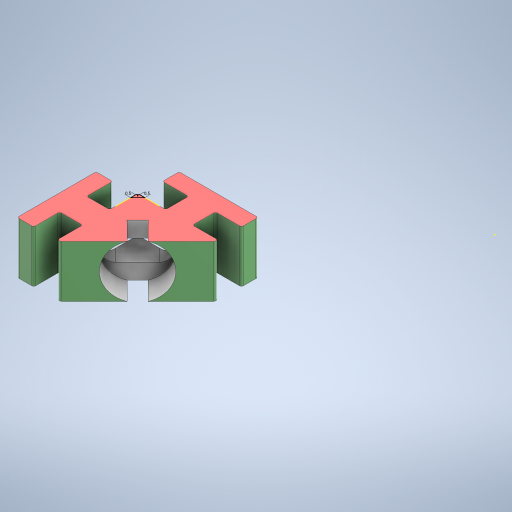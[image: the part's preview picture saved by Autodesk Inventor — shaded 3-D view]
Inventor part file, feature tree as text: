
AUTODESK INVENTOR PART (.ipt)
format: ipt  version: 2023 (Build 270158000, 158)  size: 336,384 bytes
history: native  units: in
note: dims shown in document units (in); Inventor stores cm internally (conversion verified against a paired STEP export)
features: other x4, sketch x3, extrude x2
ambient origin geometry x8: Origin, YZ Plane, XZ Plane, XY Plane, X Axis, Y Axis, Z Axis, Center Point
bodies: Body1 (feature_tree)
feature tree (9):
  other  "TmpPart3.ipt"
  extrude  "Extrusion1"  Depth=0.3937in
  extrude  "Extrusion2"  Depth=0.0591in
  sketch  "Sketch3"  dims[d5=0.0787in d6=0.126in d7=0.0in d8=0.0197in d9=0.0197in]
  other  "PLA2::TmpPart3.ipt"
  other  "TaggingFeature1"
  sketch  "Sketch1"  dims[d0=0.3937in d1=0.2047in]
  sketch  "Sketch2"  dims[d2=0.0984in d3=0.0in d4=0.0591in]
  other  "PLA2"
